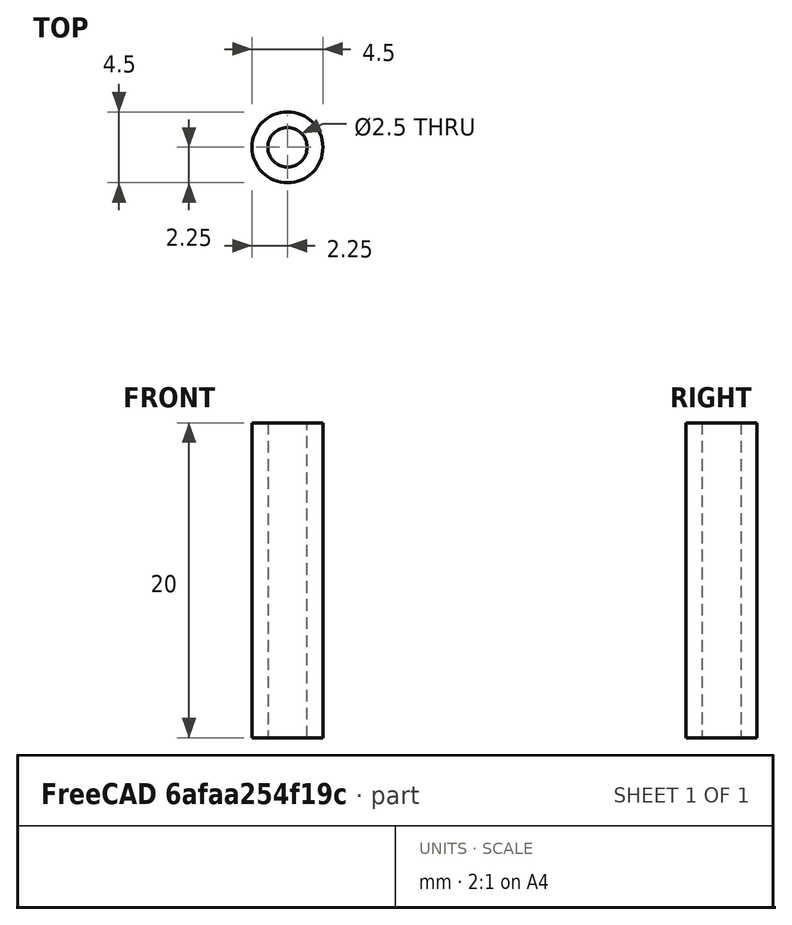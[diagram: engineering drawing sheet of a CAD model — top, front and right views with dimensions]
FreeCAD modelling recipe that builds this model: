
FCSTD DOCUMENT  (FreeCAD 1.0R39319 (Git))
Label: SpeakerStandoffs
License: All rights reserved
LicenseURL: https://en.wikipedia.org/wiki/All_rights_reserved
objects: Sketcher::SketchObject×1, PartDesign::Pad×1, PartDesign::Body×1
note: 6 computed .brp shape members not serialized (recipe doc carries the construction recipe); baked Part::Feature solids carry a one-line shape summary decoded from their .brp

FEATURE [Sketcher::SketchObject] Sketch
  ArcFitTolerance = 1e-06
  AttachmentSupport = -> [XY_Plane]
  FullyConstrained = true
  MakeInternals = false
  MapMode = 5
  sketch-geometry (2):
    g0: Circle CenterX=0 CenterY=0 CenterZ=0 NormalX=0 NormalY=0 NormalZ=1 AngleXU=0 Radius=2.25
    g1: Circle CenterX=0 CenterY=0 CenterZ=0 NormalX=0 NormalY=0 NormalZ=1 AngleXU=0 Radius=1.25
  constraints (4):
    c: Coincident(g0,g-1)
    c: Coincident(g1,g0)
    c: Distance(g1,g0) = 1
    c: Diameter(g1) = 2.5
FEATURE [PartDesign::Pad] Pad
  Direction = (0,0,1)
  Length = 20
  Length2 = 10
  Profile = -> Sketch
  ReferenceAxis = -> Sketch [N_Axis]
  Refine = true
  Suppressed = false
  Type = 0
FEATURE [PartDesign::Body] Body
  AllowCompound = false
  Group = -> [Sketch,Pad]
  Origin = -> Origin
  Tip = -> Pad
